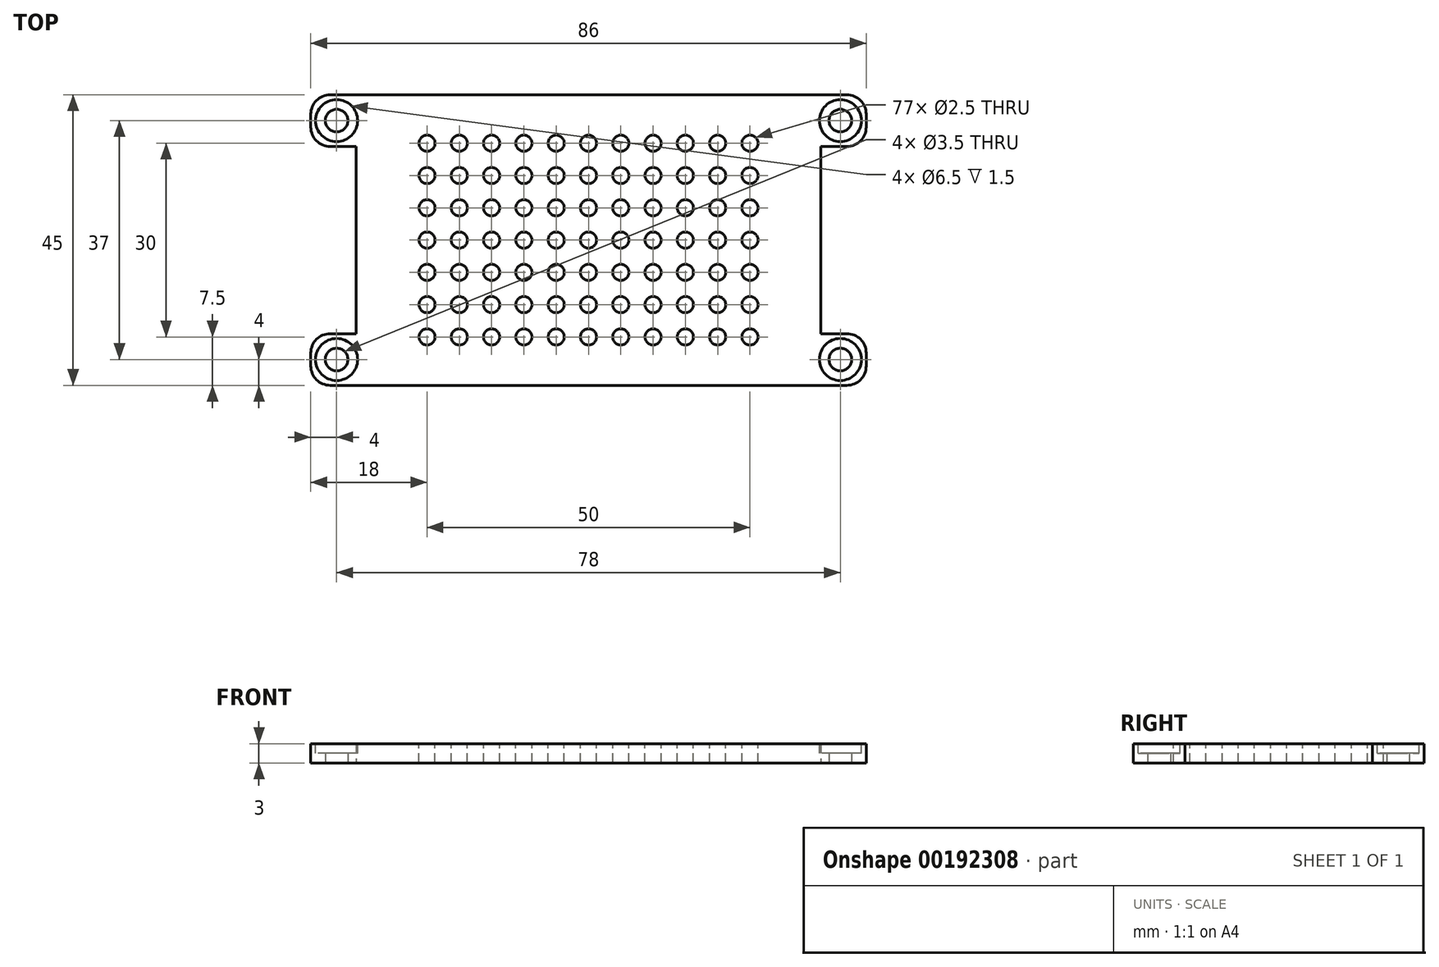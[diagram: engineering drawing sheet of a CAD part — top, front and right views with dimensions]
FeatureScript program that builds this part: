
annotation { "Feature Type Name" : "Feature", "Feature Type Description" : "" }
export const myFeature = defineFeature(function(context is Context, id is Id, definition is map)
    precondition{}
    {
        {
            var Q0;
            Q0=qCreatedBy(makeId("Top.planeOp"),FACE);
            var sketch = newSketch(context, id + "F0", { "sketchPlane" : qUnion([Q0])});
            skLineSegment(sketch, "E0", {"start": v(0, 22.5) * mm, "end": v(43, 22.5) * mm});
            skLineSegment(sketch, "E1", {"start": v(43, 22.5) * mm, "end": v(43, 14.5) * mm});
            skLineSegment(sketch, "E2", {"start": v(43, 14.5) * mm, "end": v(36, 14.5) * mm});
            skLineSegment(sketch, "E3", {"start": v(36, 14.5) * mm, "end": v(36, 0) * mm});
            skCircle(sketch, "E4", {"center": v(39, 18.5) * mm, "radius": 1.75 * mm});
            skLineSegment(sketch, "E5.MirrorCS", {"start": v(0, -22.5) * mm, "end": v(43, -22.5) * mm});
            skLineSegment(sketch, "E6.MirrorCS", {"start": v(43, -22.5) * mm, "end": v(43, -14.5) * mm});
            skCircle(sketch, "E7.MirrorC", {"center": v(39, -18.5) * mm, "radius": 1.75 * mm});
            skLineSegment(sketch, "E8.MirrorCS", {"start": v(43, -14.5) * mm, "end": v(36, -14.5) * mm});
            skLineSegment(sketch, "E9.MirrorCS", {"start": v(36, -14.5) * mm, "end": v(36, 0) * mm});
            skLineSegment(sketch, "E10.MirrorCS", {"start": v(0, 22.5) * mm, "end": v(-43, 22.5) * mm});
            skLineSegment(sketch, "E11.MirrorCS", {"start": v(-43, 22.5) * mm, "end": v(-43, 14.5) * mm});
            skCircle(sketch, "E12.MirrorC", {"center": v(-39, 18.5) * mm, "radius": 1.75 * mm});
            skLineSegment(sketch, "E13.MirrorCS", {"start": v(-43, 14.5) * mm, "end": v(-36, 14.5) * mm});
            skLineSegment(sketch, "E14.MirrorCS", {"start": v(-36, 14.5) * mm, "end": v(-36, 0) * mm});
            skLineSegment(sketch, "E15.MirrorCS", {"start": v(-36, -14.5) * mm, "end": v(-36, 0) * mm});
            skLineSegment(sketch, "E16.MirrorCS", {"start": v(-43, -14.5) * mm, "end": v(-36, -14.5) * mm});
            skLineSegment(sketch, "E17.MirrorCS", {"start": v(-43, -22.5) * mm, "end": v(-43, -14.5) * mm});
            skCircle(sketch, "E18.MirrorC", {"center": v(-39, -18.5) * mm, "radius": 1.75 * mm});
            skLineSegment(sketch, "E19.MirrorCS", {"start": v(0, -22.5) * mm, "end": v(-43, -22.5) * mm});
            skSolve(sketch);
        }
        {
            var Q0;
            Q0 = qSketchRegion(id + "F0", true);
            extrude(context, id + "F1", {"entities" : qUnion([Q0]), "depth" : 3 * mm});
        }
        {
            var Q0;
            Q0=makeQuery(id+"F1.opExtrude","CAP_FACE",FACE,{"disambiguationData":[OSD([sQuery(id+"F0.wireOp",EDGE,"E0"),sQuery(id+"F0.wireOp",EDGE,"E1"),sQuery(id+"F0.wireOp",EDGE,"E2"),sQuery(id+"F0.wireOp",EDGE,"E3"),sQuery(id+"F0.wireOp",EDGE,"E4"),sQuery(id+"F0.wireOp",EDGE,"E5.MirrorCS"),sQuery(id+"F0.wireOp",EDGE,"E6.MirrorCS"),sQuery(id+"F0.wireOp",EDGE,"E7.MirrorC"),sQuery(id+"F0.wireOp",EDGE,"E8.MirrorCS"),sQuery(id+"F0.wireOp",EDGE,"E9.MirrorCS"),sQuery(id+"F0.wireOp",EDGE,"E10.MirrorCS"),sQuery(id+"F0.wireOp",EDGE,"E11.MirrorCS"),sQuery(id+"F0.wireOp",EDGE,"E12.MirrorC"),sQuery(id+"F0.wireOp",EDGE,"E13.MirrorCS"),sQuery(id+"F0.wireOp",EDGE,"E14.MirrorCS"),sQuery(id+"F0.wireOp",EDGE,"E15.MirrorCS"),sQuery(id+"F0.wireOp",EDGE,"E16.MirrorCS"),sQuery(id+"F0.wireOp",EDGE,"E17.MirrorCS"),sQuery(id+"F0.wireOp",EDGE,"E18.MirrorC"),sQuery(id+"F0.wireOp",EDGE,"E19.MirrorCS")])],"isStart":false});
            var sketch = newSketch(context, id + "F2", { "sketchPlane" : qUnion([Q0])});
            skCircle(sketch, "E20", {"center": v(-39, 18.5) * mm, "radius": 3.25 * mm});
            skCircle(sketch, "E21", {"center": v(-39, -18.5) * mm, "radius": 3.25 * mm});
            skCircle(sketch, "E22", {"center": v(39, 18.5) * mm, "radius": 3.25 * mm});
            skCircle(sketch, "E23", {"center": v(39, -18.5) * mm, "radius": 3.25 * mm});
            skSolve(sketch);
        }
        {
            var Q0;
            Q0 = qSketchRegion(id + "F2", true);
            extrude(context, id + "F3", {"entities" : qUnion([Q0]), "operationType" : NewBodyOperationType.REMOVE, "oppositeDirection" : true, "depth" : 1.5 * mm});
        }
        {
            var Q0;
            Q0=makeQuery(id+"F1.opExtrude","SWEPT_EDGE",EDGE,{"disambiguationData":[OSD([sQuery(id+"F0.wireOp",EDGE,"E5.MirrorCS"),sQuery(id+"F0.wireOp",EDGE,"E6.MirrorCS")])]});
            var Q1;
            Q1=makeQuery(id+"F1.opExtrude","SWEPT_EDGE",EDGE,{"disambiguationData":[OSD([sQuery(id+"F0.wireOp",EDGE,"E6.MirrorCS"),sQuery(id+"F0.wireOp",EDGE,"E8.MirrorCS")])]});
            var Q2;
            Q2=makeQuery(id+"F1.opExtrude","SWEPT_EDGE",EDGE,{"disambiguationData":[OSD([sQuery(id+"F0.wireOp",EDGE,"E1"),sQuery(id+"F0.wireOp",EDGE,"E2")])]});
            var Q3;
            Q3=makeQuery(id+"F1.opExtrude","SWEPT_EDGE",EDGE,{"disambiguationData":[OSD([sQuery(id+"F0.wireOp",EDGE,"E0"),sQuery(id+"F0.wireOp",EDGE,"E1")])]});
            var Q4;
            Q4=makeQuery(id+"F1.opExtrude","SWEPT_EDGE",EDGE,{"disambiguationData":[OSD([sQuery(id+"F0.wireOp",EDGE,"E16.MirrorCS"),sQuery(id+"F0.wireOp",EDGE,"E17.MirrorCS")])]});
            var Q5;
            Q5=makeQuery(id+"F1.opExtrude","SWEPT_EDGE",EDGE,{"disambiguationData":[OSD([sQuery(id+"F0.wireOp",EDGE,"E17.MirrorCS"),sQuery(id+"F0.wireOp",EDGE,"E19.MirrorCS")])]});
            var Q6;
            Q6=makeQuery(id+"F1.opExtrude","SWEPT_EDGE",EDGE,{"disambiguationData":[OSD([sQuery(id+"F0.wireOp",EDGE,"E11.MirrorCS"),sQuery(id+"F0.wireOp",EDGE,"E13.MirrorCS")])]});
            var Q7;
            Q7=makeQuery(id+"F1.opExtrude","SWEPT_EDGE",EDGE,{"disambiguationData":[OSD([sQuery(id+"F0.wireOp",EDGE,"E10.MirrorCS"),sQuery(id+"F0.wireOp",EDGE,"E11.MirrorCS")])]});
            fillet(context, id + "F4", {"entities" : qUnion([Q0, Q1, Q2, Q3, Q4, Q5, Q6, Q7]), "radius" : 3 * mm, "tangentPropagation" : true, "allowEdgeOverflow" : false});
        }
        {
            var Q0;
            Q0=makeQuery(id+"F1.opExtrude","CAP_FACE",FACE,{"disambiguationData":[OSD([sQuery(id+"F0.wireOp",EDGE,"E0"),sQuery(id+"F0.wireOp",EDGE,"E1"),sQuery(id+"F0.wireOp",EDGE,"E2"),sQuery(id+"F0.wireOp",EDGE,"E3"),sQuery(id+"F0.wireOp",EDGE,"E4"),sQuery(id+"F0.wireOp",EDGE,"E5.MirrorCS"),sQuery(id+"F0.wireOp",EDGE,"E6.MirrorCS"),sQuery(id+"F0.wireOp",EDGE,"E7.MirrorC"),sQuery(id+"F0.wireOp",EDGE,"E8.MirrorCS"),sQuery(id+"F0.wireOp",EDGE,"E9.MirrorCS"),sQuery(id+"F0.wireOp",EDGE,"E10.MirrorCS"),sQuery(id+"F0.wireOp",EDGE,"E11.MirrorCS"),sQuery(id+"F0.wireOp",EDGE,"E12.MirrorC"),sQuery(id+"F0.wireOp",EDGE,"E13.MirrorCS"),sQuery(id+"F0.wireOp",EDGE,"E14.MirrorCS"),sQuery(id+"F0.wireOp",EDGE,"E15.MirrorCS"),sQuery(id+"F0.wireOp",EDGE,"E16.MirrorCS"),sQuery(id+"F0.wireOp",EDGE,"E17.MirrorCS"),sQuery(id+"F0.wireOp",EDGE,"E18.MirrorC"),sQuery(id+"F0.wireOp",EDGE,"E19.MirrorCS")])],"isStart":false});
            var sketch = newSketch(context, id + "F5", { "sketchPlane" : qUnion([Q0])});
            skCircle(sketch, "E24", {"center": v(-25, 15) * mm, "radius": 1.25 * mm});
            skCircle(sketch, "E25.1.0.0", {"center": v(-20, 15) * mm, "radius": 1.25 * mm});
            skCircle(sketch, "E25.2.0.0", {"center": v(-15, 15) * mm, "radius": 1.25 * mm});
            skCircle(sketch, "E25.3.0.0", {"center": v(-10, 15) * mm, "radius": 1.25 * mm});
            skCircle(sketch, "E25.4.0.0", {"center": v(-5, 15) * mm, "radius": 1.25 * mm});
            skCircle(sketch, "E25.5.0.0", {"center": v(0, 15) * mm, "radius": 1.25 * mm});
            skCircle(sketch, "E25.6.0.0", {"center": v(5, 15) * mm, "radius": 1.25 * mm});
            skCircle(sketch, "E25.7.0.0", {"center": v(10, 15) * mm, "radius": 1.25 * mm});
            skCircle(sketch, "E25.8.0.0", {"center": v(15, 15) * mm, "radius": 1.25 * mm});
            skCircle(sketch, "E25.9.0.0", {"center": v(20, 15) * mm, "radius": 1.25 * mm});
            skCircle(sketch, "E25.10.0.0", {"center": v(25, 15) * mm, "radius": 1.25 * mm});
            skLineSegment(sketch, "E25.direction1", {"start": v(-25, 15) * mm, "end": v(-20, 15) * mm, "construction": true});
            skCircle(sketch, "E26.1.0.0", {"center": v(-25, 10) * mm, "radius": 1.25 * mm});
            skCircle(sketch, "E26.1.0.1", {"center": v(-20, 10) * mm, "radius": 1.25 * mm});
            skCircle(sketch, "E26.1.0.2", {"center": v(-15, 10) * mm, "radius": 1.25 * mm});
            skCircle(sketch, "E26.1.0.3", {"center": v(-10, 10) * mm, "radius": 1.25 * mm});
            skCircle(sketch, "E26.1.0.4", {"center": v(-5, 10) * mm, "radius": 1.25 * mm});
            skCircle(sketch, "E26.1.0.5", {"center": v(0, 10) * mm, "radius": 1.25 * mm});
            skCircle(sketch, "E26.1.0.6", {"center": v(5, 10) * mm, "radius": 1.25 * mm});
            skCircle(sketch, "E26.1.0.7", {"center": v(10, 10) * mm, "radius": 1.25 * mm});
            skCircle(sketch, "E26.1.0.8", {"center": v(15, 10) * mm, "radius": 1.25 * mm});
            skCircle(sketch, "E26.1.0.9", {"center": v(20, 10) * mm, "radius": 1.25 * mm});
            skCircle(sketch, "E26.1.0.10", {"center": v(25, 10) * mm, "radius": 1.25 * mm});
            skCircle(sketch, "E26.2.0.0", {"center": v(-25, 5) * mm, "radius": 1.25 * mm});
            skCircle(sketch, "E26.2.0.1", {"center": v(-20, 5) * mm, "radius": 1.25 * mm});
            skCircle(sketch, "E26.2.0.2", {"center": v(-15, 5) * mm, "radius": 1.25 * mm});
            skCircle(sketch, "E26.2.0.3", {"center": v(-10, 5) * mm, "radius": 1.25 * mm});
            skCircle(sketch, "E26.2.0.4", {"center": v(-5, 5) * mm, "radius": 1.25 * mm});
            skCircle(sketch, "E26.2.0.5", {"center": v(0, 5) * mm, "radius": 1.25 * mm});
            skCircle(sketch, "E26.2.0.6", {"center": v(5, 5) * mm, "radius": 1.25 * mm});
            skCircle(sketch, "E26.2.0.7", {"center": v(10, 5) * mm, "radius": 1.25 * mm});
            skCircle(sketch, "E26.2.0.8", {"center": v(15, 5) * mm, "radius": 1.25 * mm});
            skCircle(sketch, "E26.2.0.9", {"center": v(20, 5) * mm, "radius": 1.25 * mm});
            skCircle(sketch, "E26.2.0.10", {"center": v(25, 5) * mm, "radius": 1.25 * mm});
            skCircle(sketch, "E26.3.0.0", {"center": v(-25, 0) * mm, "radius": 1.25 * mm});
            skCircle(sketch, "E26.3.0.1", {"center": v(-20, 0) * mm, "radius": 1.25 * mm});
            skCircle(sketch, "E26.3.0.2", {"center": v(-15, 0) * mm, "radius": 1.25 * mm});
            skCircle(sketch, "E26.3.0.3", {"center": v(-10, 0) * mm, "radius": 1.25 * mm});
            skCircle(sketch, "E26.3.0.4", {"center": v(-5, 0) * mm, "radius": 1.25 * mm});
            skCircle(sketch, "E26.3.0.5", {"center": v(0, 0) * mm, "radius": 1.25 * mm});
            skCircle(sketch, "E26.3.0.6", {"center": v(5, 0) * mm, "radius": 1.25 * mm});
            skCircle(sketch, "E26.3.0.7", {"center": v(10, 0) * mm, "radius": 1.25 * mm});
            skCircle(sketch, "E26.3.0.8", {"center": v(15, 0) * mm, "radius": 1.25 * mm});
            skCircle(sketch, "E26.3.0.9", {"center": v(20, 0) * mm, "radius": 1.25 * mm});
            skCircle(sketch, "E26.3.0.10", {"center": v(25, 0) * mm, "radius": 1.25 * mm});
            skCircle(sketch, "E26.4.0.0", {"center": v(-25, -5) * mm, "radius": 1.25 * mm});
            skCircle(sketch, "E26.4.0.1", {"center": v(-20, -5) * mm, "radius": 1.25 * mm});
            skCircle(sketch, "E26.4.0.2", {"center": v(-15, -5) * mm, "radius": 1.25 * mm});
            skCircle(sketch, "E26.4.0.3", {"center": v(-10, -5) * mm, "radius": 1.25 * mm});
            skCircle(sketch, "E26.4.0.4", {"center": v(-5, -5) * mm, "radius": 1.25 * mm});
            skCircle(sketch, "E26.4.0.5", {"center": v(0, -5) * mm, "radius": 1.25 * mm});
            skCircle(sketch, "E26.4.0.6", {"center": v(5, -5) * mm, "radius": 1.25 * mm});
            skCircle(sketch, "E26.4.0.7", {"center": v(10, -5) * mm, "radius": 1.25 * mm});
            skCircle(sketch, "E26.4.0.8", {"center": v(15, -5) * mm, "radius": 1.25 * mm});
            skCircle(sketch, "E26.4.0.9", {"center": v(20, -5) * mm, "radius": 1.25 * mm});
            skCircle(sketch, "E26.4.0.10", {"center": v(25, -5) * mm, "radius": 1.25 * mm});
            skCircle(sketch, "E26.5.0.0", {"center": v(-25, -10) * mm, "radius": 1.25 * mm});
            skCircle(sketch, "E26.5.0.1", {"center": v(-20, -10) * mm, "radius": 1.25 * mm});
            skCircle(sketch, "E26.5.0.2", {"center": v(-15, -10) * mm, "radius": 1.25 * mm});
            skCircle(sketch, "E26.5.0.3", {"center": v(-10, -10) * mm, "radius": 1.25 * mm});
            skCircle(sketch, "E26.5.0.4", {"center": v(-5, -10) * mm, "radius": 1.25 * mm});
            skCircle(sketch, "E26.5.0.5", {"center": v(0, -10) * mm, "radius": 1.25 * mm});
            skCircle(sketch, "E26.5.0.6", {"center": v(5, -10) * mm, "radius": 1.25 * mm});
            skCircle(sketch, "E26.5.0.7", {"center": v(10, -10) * mm, "radius": 1.25 * mm});
            skCircle(sketch, "E26.5.0.8", {"center": v(15, -10) * mm, "radius": 1.25 * mm});
            skCircle(sketch, "E26.5.0.9", {"center": v(20, -10) * mm, "radius": 1.25 * mm});
            skCircle(sketch, "E26.5.0.10", {"center": v(25, -10) * mm, "radius": 1.25 * mm});
            skCircle(sketch, "E26.6.0.0", {"center": v(-25, -15) * mm, "radius": 1.25 * mm});
            skCircle(sketch, "E26.6.0.1", {"center": v(-20, -15) * mm, "radius": 1.25 * mm});
            skCircle(sketch, "E26.6.0.2", {"center": v(-15, -15) * mm, "radius": 1.25 * mm});
            skCircle(sketch, "E26.6.0.3", {"center": v(-10, -15) * mm, "radius": 1.25 * mm});
            skCircle(sketch, "E26.6.0.4", {"center": v(-5, -15) * mm, "radius": 1.25 * mm});
            skCircle(sketch, "E26.6.0.5", {"center": v(0, -15) * mm, "radius": 1.25 * mm});
            skCircle(sketch, "E26.6.0.6", {"center": v(5, -15) * mm, "radius": 1.25 * mm});
            skCircle(sketch, "E26.6.0.7", {"center": v(10, -15) * mm, "radius": 1.25 * mm});
            skCircle(sketch, "E26.6.0.8", {"center": v(15, -15) * mm, "radius": 1.25 * mm});
            skCircle(sketch, "E26.6.0.9", {"center": v(20, -15) * mm, "radius": 1.25 * mm});
            skCircle(sketch, "E26.6.0.10", {"center": v(25, -15) * mm, "radius": 1.25 * mm});
            skLineSegment(sketch, "E26.direction1", {"start": v(-25, 15) * mm, "end": v(-25, 10) * mm, "construction": true});
            skSolve(sketch);
        }
        {
            var Q0;
            Q0 = qSketchRegion(id + "F5", true);
            extrude(context, id + "F6", {"entities" : qUnion([Q0]), "operationType" : NewBodyOperationType.REMOVE, "endBound" : BoundingType.THROUGH_ALL, "oppositeDirection" : true, "depth" : 25 * mm});
        }
    });
